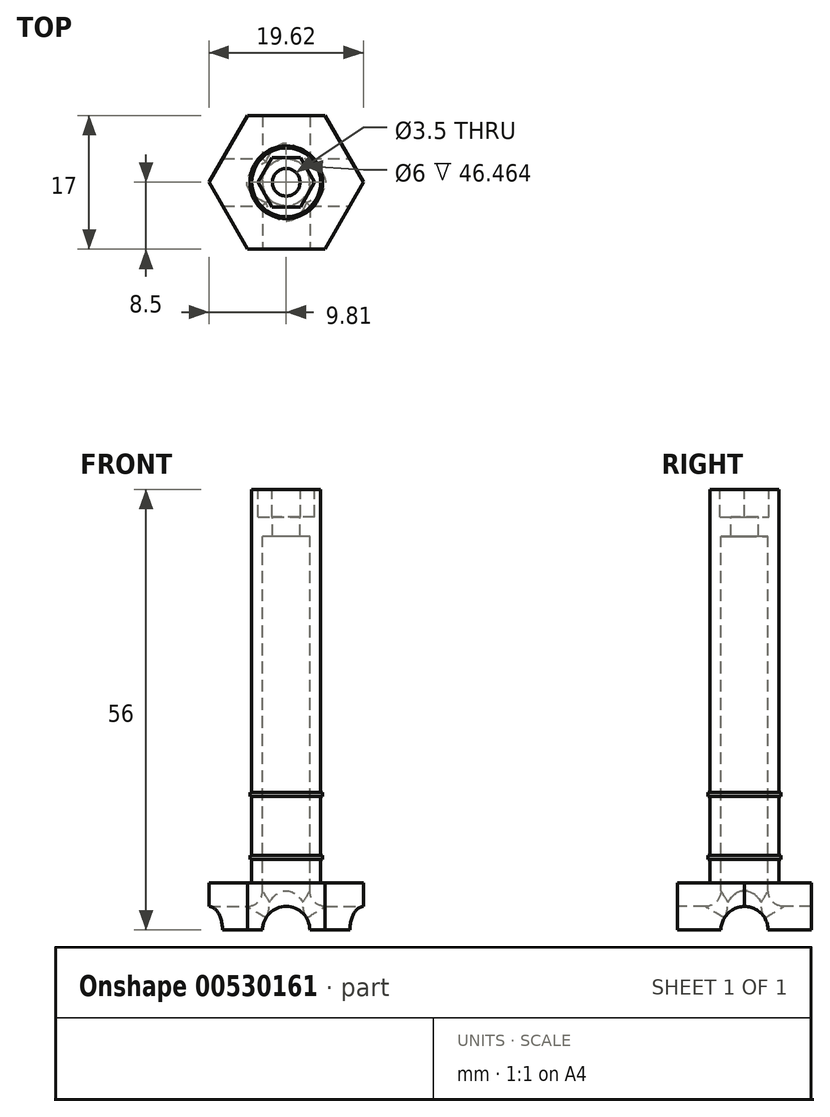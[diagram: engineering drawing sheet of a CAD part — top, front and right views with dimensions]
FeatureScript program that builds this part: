
annotation { "Feature Type Name" : "Feature", "Feature Type Description" : "" }
export const myFeature = defineFeature(function(context is Context, id is Id, definition is map)
    precondition{}
    {
        {
            var Q0;
            Q0=qCreatedBy(makeId("Top.planeOp"),FACE);
            var sketch = newSketch(context, id + "F0", { "sketchPlane" : qUnion([Q0])});
            skCircle(sketch, "E0.cCircle", {"center": v(0, 0) * mm, "radius": 8.5 * mm, "construction": true});
            skLineSegment(sketch, "E0.0", {"start": v(-4.9, 8.5) * mm, "end": v(4.9, 8.5) * mm});
            skLineSegment(sketch, "E0.1", {"start": v(4.9, 8.5) * mm, "end": v(9.81, 0) * mm});
            skLineSegment(sketch, "E0.2", {"start": v(9.81, 0) * mm, "end": v(4.9, -8.5) * mm});
            skLineSegment(sketch, "E0.3", {"start": v(4.9, -8.5) * mm, "end": v(-4.9, -8.5) * mm});
            skLineSegment(sketch, "E0.4", {"start": v(-4.9, -8.5) * mm, "end": v(-9.81, 0) * mm});
            skLineSegment(sketch, "E0.5", {"start": v(-9.81, 0) * mm, "end": v(-4.9, 8.5) * mm});
            skPoint(sketch, "E0.0.midPoint", {"position": v(0, 8.5) * mm});
            skSolve(sketch);
        }
        {
            var Q0;
            Q0=makeQuery(id+"F0.imprint","IMPRINT",FACE,{"disambiguationData":[TD([[makeQuery(id+"F0.imprint","IMPRINT",EDGE,{"derivedFrom":sQuery(id+"F0.wireOp",EDGE,"E0.0")}),-1.0]])]});
            extrude(context, id + "F1", {"entities" : qUnion([Q0]), "depth" : 6 * mm, "offsetDistance" : 25 * mm});
        }
        {
            var Q0;
            Q0=makeQuery(id+"F1.opExtrude","CAP_FACE",FACE,{"disambiguationData":[OSD([sQuery(id+"F0.wireOp",EDGE,"E0.0"),sQuery(id+"F0.wireOp",EDGE,"E0.1"),sQuery(id+"F0.wireOp",EDGE,"E0.2"),sQuery(id+"F0.wireOp",EDGE,"E0.3"),sQuery(id+"F0.wireOp",EDGE,"E0.4"),sQuery(id+"F0.wireOp",EDGE,"E0.5")])],"isStart":false});
            var sketch = newSketch(context, id + "F2", { "sketchPlane" : qUnion([Q0])});
            skCircle(sketch, "E1", {"center": v(0, 0) * mm, "radius": 4.38 * mm});
            skCircle(sketch, "E2", {"center": v(0, 0) * mm, "radius": 4.63 * mm});
            skSolve(sketch);
        }
        {
            var Q0;
            Q0=makeQuery(id+"F2.imprint","IMPRINT",FACE,{"disambiguationData":[TD([[makeQuery(id+"F2.imprint","IMPRINT",EDGE,{"derivedFrom":sQuery(id+"F2.wireOp",EDGE,"E1")}),1.0]])]});
            extrude(context, id + "F3", {"entities" : qUnion([Q0]), "operationType" : NewBodyOperationType.ADD, "depth" : 50 * mm, "offsetDistance" : 25 * mm});
        }
        {
            var Q0;
            Q0=makeQuery(id+"F2.imprint","IMPRINT",FACE,{"disambiguationData":[TD([[makeQuery(id+"F2.imprint","IMPRINT",EDGE,{"derivedFrom":sQuery(id+"F2.wireOp",EDGE,"E1")}),-1.0]])]});
            extrude(context, id + "F4", {"entities" : qUnion([Q0]), "operationType" : NewBodyOperationType.ADD, "depth" : 3.5 * mm, "offsetDistance" : 25 * mm, "hasSecondDirection" : true, "secondDirectionOppositeDirection" : false, "secondDirectionDepth" : 3 * mm});
        }
        {
            var Q0;
            Q0=makeQuery(id+"F2.imprint","IMPRINT",FACE,{"disambiguationData":[TD([[makeQuery(id+"F2.imprint","IMPRINT",EDGE,{"derivedFrom":sQuery(id+"F2.wireOp",EDGE,"E1")}),-1.0]])]});
            extrude(context, id + "F5", {"entities" : qUnion([Q0]), "operationType" : NewBodyOperationType.ADD, "depth" : 11.5 * mm, "offsetDistance" : 25 * mm, "hasSecondDirection" : true, "secondDirectionOppositeDirection" : false, "secondDirectionDepth" : 11 * mm});
        }
        {
            var Q0;
            Q0=makeQuery(id+"F3.opExtrude","CAP_FACE",FACE,{"disambiguationData":[OSD([sQuery(id+"F2.wireOp",EDGE,"E1")])],"isStart":false});
            var sketch = newSketch(context, id + "F6", { "sketchPlane" : qUnion([Q0])});
            skCircle(sketch, "E3.cCircle", {"center": v(0, 0) * mm, "radius": 3.12 * mm, "construction": true});
            skLineSegment(sketch, "E3.0", {"start": v(-1.8, 3.12) * mm, "end": v(1.8, 3.12) * mm});
            skLineSegment(sketch, "E3.1", {"start": v(1.8, 3.12) * mm, "end": v(3.6, 0) * mm});
            skLineSegment(sketch, "E3.2", {"start": v(3.6, 0) * mm, "end": v(1.8, -3.12) * mm});
            skLineSegment(sketch, "E3.3", {"start": v(1.8, -3.12) * mm, "end": v(-1.8, -3.13) * mm});
            skLineSegment(sketch, "E3.4", {"start": v(-1.8, -3.13) * mm, "end": v(-3.6, 0) * mm});
            skLineSegment(sketch, "E3.5", {"start": v(-3.6, 0) * mm, "end": v(-1.8, 3.12) * mm});
            skPoint(sketch, "E3.0.midPoint", {"position": v(0, 3.12) * mm});
            skSolve(sketch);
        }
        {
            var Q0;
            Q0=makeQuery(id+"F6.imprint","IMPRINT",FACE,{"disambiguationData":[TD([[makeQuery(id+"F6.imprint","IMPRINT",EDGE,{"derivedFrom":sQuery(id+"F6.wireOp",EDGE,"E3.0")}),-1.0]])]});
            extrude(context, id + "F7", {"entities" : qUnion([Q0]), "operationType" : NewBodyOperationType.REMOVE, "oppositeDirection" : true, "depth" : 3.5 * mm, "offsetDistance" : 25 * mm});
        }
        {
            var Q0;
            Q0=makeQuery(id+"F3.opExtrude","CAP_FACE",FACE,{"disambiguationData":[OSD([sQuery(id+"F2.wireOp",EDGE,"E1")])],"isStart":false});
            var sketch = newSketch(context, id + "F8", { "sketchPlane" : qUnion([Q0])});
            skCircle(sketch, "E4", {"center": v(0, 0) * mm, "radius": 1.75 * mm});
            skSolve(sketch);
        }
        {
            var Q0;
            Q0=makeQuery(id+"F8.imprint","IMPRINT",FACE,{"disambiguationData":[TD([[makeQuery(id+"F8.imprint","IMPRINT",EDGE,{"derivedFrom":sQuery(id+"F8.wireOp",EDGE,"E4")}),1.0]])]});
            extrude(context, id + "F9", {"entities" : qUnion([Q0]), "operationType" : NewBodyOperationType.REMOVE, "endBound" : BoundingType.THROUGH_ALL, "oppositeDirection" : true, "depth" : 25 * mm, "offsetDistance" : 25 * mm});
        }
        {
            var Q0;
            Q0=makeQuery(id+"F3.opExtrude","CAP_FACE",FACE,{"disambiguationData":[OSD([sQuery(id+"F2.wireOp",EDGE,"E1")])],"isStart":false});
            var sketch = newSketch(context, id + "F10", { "sketchPlane" : qUnion([Q0])});
            skCircle(sketch, "E5", {"center": v(0, 0) * mm, "radius": 3 * mm});
            skSolve(sketch);
        }
        {
            var Q0;
            Q0 = qSketchRegion(id + "F10", true);
            var Q1;
            Q1=makeQuery(id+"F1.opExtrude","CAP_FACE",FACE,{"disambiguationData":[OSD([sQuery(id+"F0.wireOp",EDGE,"E0.0"),sQuery(id+"F0.wireOp",EDGE,"E0.1"),sQuery(id+"F0.wireOp",EDGE,"E0.2"),sQuery(id+"F0.wireOp",EDGE,"E0.3"),sQuery(id+"F0.wireOp",EDGE,"E0.4"),sQuery(id+"F0.wireOp",EDGE,"E0.5")])],"isStart":true});
            extrude(context, id + "F11", {"entities" : qUnion([Q0]), "operationType" : NewBodyOperationType.REMOVE, "endBound" : BoundingType.UP_TO_SURFACE, "oppositeDirection" : true, "depth" : 25 * mm, "endBoundEntityFace" : qUnion([Q1]), "offsetDistance" : 25 * mm, "hasSecondDirection" : true, "secondDirectionOppositeDirection" : true, "secondDirectionDepth" : 6 * mm});
        }
        {
            var Q0;
            Q0=qCreatedBy(makeId("Front.planeOp"),FACE);
            var sketch = newSketch(context, id + "F12", { "sketchPlane" : qUnion([Q0])});
            skCircle(sketch, "E6", {"center": v(0, 0) * mm, "radius": 3 * mm});
            skSolve(sketch);
        }
        {
            var Q0;
            Q0 = qSketchRegion(id + "F12", true);
            var Q1;
            Q1=makeQuery(id+"F1.opExtrude","SWEPT_FACE",FACE,{"disambiguationData":[OSD([sQuery(id+"F0.wireOp",EDGE,"E0.0")])]});
            var Q2;
            Q2=makeQuery(id+"F1.opExtrude","SWEPT_FACE",FACE,{"disambiguationData":[OSD([sQuery(id+"F0.wireOp",EDGE,"E0.3")])]});
            extrude(context, id + "F13", {"entities" : qUnion([Q0]), "operationType" : NewBodyOperationType.REMOVE, "oppositeDirection" : true, "depth" : 25 * mm, "endBoundEntityFace" : qUnion([Q1]), "offsetDistance" : 25 * mm, "symmetric" : true});
        }
        {
            var Q0;
            Q0=qCreatedBy(makeId("Right.planeOp"),FACE);
            var sketch = newSketch(context, id + "F14", { "sketchPlane" : qUnion([Q0])});
            skCircle(sketch, "E7", {"center": v(0, 0) * mm, "radius": 3 * mm});
            skSolve(sketch);
        }
        {
            var Q0;
            Q0 = qSketchRegion(id + "F14", true);
            extrude(context, id + "F15", {"entities" : qUnion([Q0]), "operationType" : NewBodyOperationType.REMOVE, "oppositeDirection" : true, "depth" : 25 * mm, "offsetDistance" : 25 * mm, "symmetric" : true});
        }
        {
            var Q0;
            Q0=makeQuery(id+"F15.boolean.opBoolean","SPLIT",EDGE,{"disambiguationData":[OD(1.0)],"derivedFrom":makeQuery(id+"F13.boolean.opBoolean","INTERSECT",EDGE,{"derivedFrom":[makeQuery(id+"F11.boolean.opBoolean","COPY",FACE,{"derivedFrom":makeQuery(id+"F11.opExtrude","SWEPT_FACE",FACE,{"disambiguationData":[OSD([sQuery(id+"F10.wireOp",EDGE,"E5")])]})}),makeQuery(id+"F13.opExtrude","SWEPT_FACE",FACE,{"disambiguationData":[OSD([sQuery(id+"F12.wireOp",EDGE,"E6")])]})]})});
            var Q1;
            Q1=makeQuery(id+"F15.boolean.opBoolean","INTERSECT",EDGE,{"disambiguationData":[OD(1.0)],"derivedFrom":[makeQuery(id+"F11.boolean.opBoolean","COPY",FACE,{"derivedFrom":makeQuery(id+"F11.opExtrude","SWEPT_FACE",FACE,{"disambiguationData":[OSD([sQuery(id+"F10.wireOp",EDGE,"E5")])]})}),makeQuery(id+"F15.opExtrude","SWEPT_FACE",FACE,{"disambiguationData":[OSD([sQuery(id+"F14.wireOp",EDGE,"E7")])]})]});
            var Q2;
            Q2=makeQuery(id+"F15.boolean.opBoolean","SPLIT",EDGE,{"disambiguationData":[OD(0.0)],"derivedFrom":makeQuery(id+"F13.boolean.opBoolean","INTERSECT",EDGE,{"derivedFrom":[makeQuery(id+"F11.boolean.opBoolean","COPY",FACE,{"derivedFrom":makeQuery(id+"F11.opExtrude","SWEPT_FACE",FACE,{"disambiguationData":[OSD([sQuery(id+"F10.wireOp",EDGE,"E5")])]})}),makeQuery(id+"F13.opExtrude","SWEPT_FACE",FACE,{"disambiguationData":[OSD([sQuery(id+"F12.wireOp",EDGE,"E6")])]})]})});
            var Q3;
            Q3=makeQuery(id+"F15.boolean.opBoolean","INTERSECT",EDGE,{"disambiguationData":[OD(0.0)],"derivedFrom":[makeQuery(id+"F11.boolean.opBoolean","COPY",FACE,{"derivedFrom":makeQuery(id+"F11.opExtrude","SWEPT_FACE",FACE,{"disambiguationData":[OSD([sQuery(id+"F10.wireOp",EDGE,"E5")])]})}),makeQuery(id+"F15.opExtrude","SWEPT_FACE",FACE,{"disambiguationData":[OSD([sQuery(id+"F14.wireOp",EDGE,"E7")])]})]});
            fillet(context, id + "F16", {"entities" : qUnion([Q0, Q1, Q2, Q3]), "tangentPropagation" : true, "radius" : 2 * mm, "defaultsChanged" : false, "vertexSettings" : [], "allowEdgeOverflow" : false});
        }
    });
